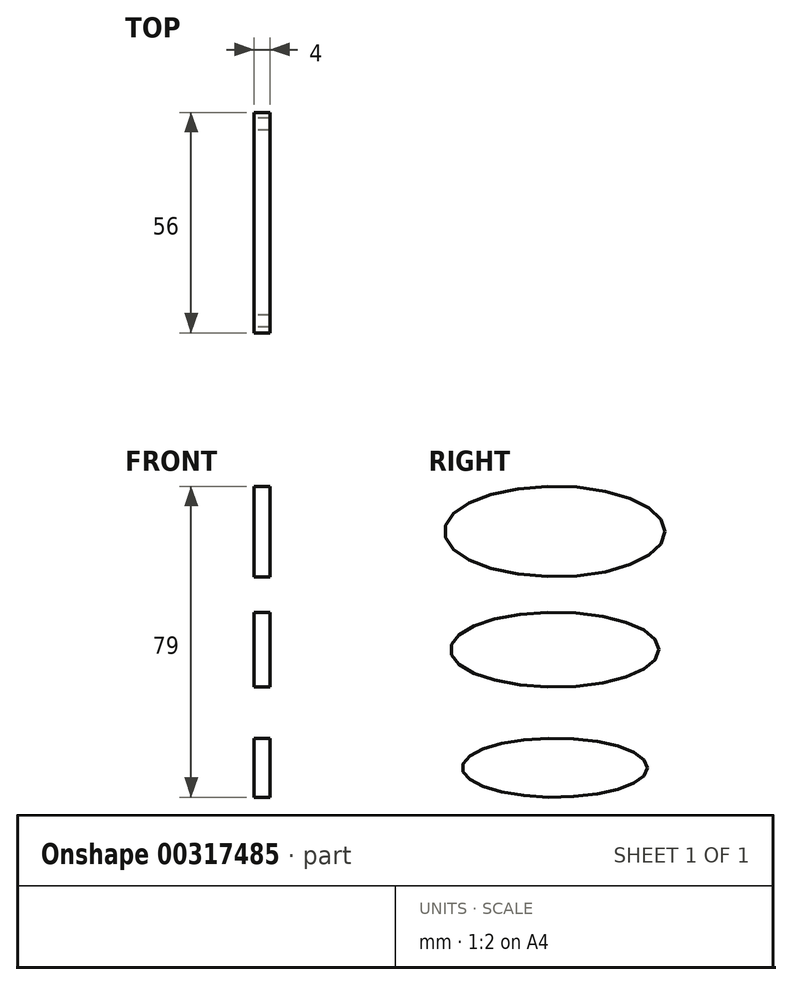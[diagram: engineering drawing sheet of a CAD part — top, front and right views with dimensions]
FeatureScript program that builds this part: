
annotation { "Feature Type Name" : "Feature", "Feature Type Description" : "" }
export const myFeature = defineFeature(function(context is Context, id is Id, definition is map)
    precondition{}
    {
        {
            var Q0;
            Q0=qCreatedBy(makeId("Right.planeOp"),FACE);
            var sketch = newSketch(context, id + "F0", { "sketchPlane" : qUnion([Q0])});
            skEllipse(sketch, "E0", {"center": v(0, 30) * mm, "majorRadius": 26.5 * mm, "minorRadius": 9.5 * mm, "majorAxis": v(1, 0)});
            skEllipse(sketch, "E1", {"center": v(0, 0) * mm, "majorRadius": 23.5 * mm, "minorRadius": 7.5 * mm, "majorAxis": v(1, 0)});
            skEllipse(sketch, "E2", {"center": v(0, 60) * mm, "majorRadius": 28 * mm, "minorRadius": 11.5 * mm, "majorAxis": v(1, 0)});
            skSolve(sketch);
        }
        {
            var Q0;
            Q0 = qSketchRegion(id + "F0", true);
            extrude(context, id + "F1", {"entities" : qUnion([Q0]), "depth" : 4 * mm, "symmetric" : true});
        }
    });
